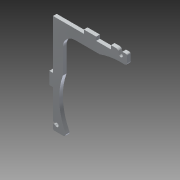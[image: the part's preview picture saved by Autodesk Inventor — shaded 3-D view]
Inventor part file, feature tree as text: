
AUTODESK INVENTOR PART (.ipt)
format: ipt  version: 2013 (Build 170138000, 138)  size: 164,864 bytes
history: native  units: mm
features: extrude x1, sketch x1
ambient origin geometry x8: Origin, YZ Plane, XZ Plane, XY Plane, X Axis, Y Axis, Z Axis, Center Point
feature tree (2):
  extrude  "Extrusion3"  Depth=10.0mm
  sketch  "Sketch2"  dims[d0=100.0mm d5=10.0mm d6=10.0mm d13=40.0mm d14=25.0mm d15=3.0mm d16=3.0mm d17=3.0mm d18=3.0mm d22=55.0mm d23=55.0mm d31=3.0mm d33=135.0deg d34=45.0deg d35=135.0deg d36=45.0deg d37=3.0mm d43=12.0mm d44=3.0mm d46=3.0mm d48=3.0mm d50=45.0deg d51=135.0deg d53=2.0mm d54=1.0mm d57=80.0mm d58=3.0mm d59=5.0mm d60=3.0mm d61=3.0mm d62=135.0deg d63=45.0deg d64=1.0mm d65=2.0mm d66=1.0mm d67=3.0mm d75=4.050253mm d76=60.0mm d78=5.0mm d79=3.0mm d85=3.0mm d86=0.0mm d87=60.0deg d92=8.0mm d93=50.0mm d94=50.0mm d95=8.0mm d96=10.0mm d97=2.0mm d98=2.0mm]
